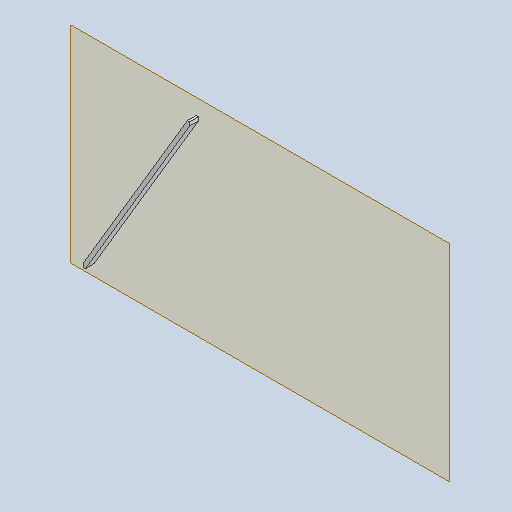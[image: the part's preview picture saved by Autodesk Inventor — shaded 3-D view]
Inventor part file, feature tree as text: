
AUTODESK INVENTOR PART (.ipt)
format: ipt  version: 2025.1 (Build 291241020, 241B)  size: 85,504 bytes
history: native  units: in
note: dims shown in document units (in); Inventor stores cm internally (conversion verified against a paired STEP export)
features: other x3, sketch x1, plane x1
ambient origin geometry x8: Origin, YZ Plane, XZ Plane, XY Plane, X Axis, Y Axis, Z Axis, Center Point
bodies: Solid1 (feature_tree)
feature tree (5):
  other  "Part11.ipt"
  other  "Solid1::Part11.ipt"
  other  "TaggingFeature1"
  sketch  "Sketch1"  dims[d0=0.3937in]
  plane  "Work Plane1"
